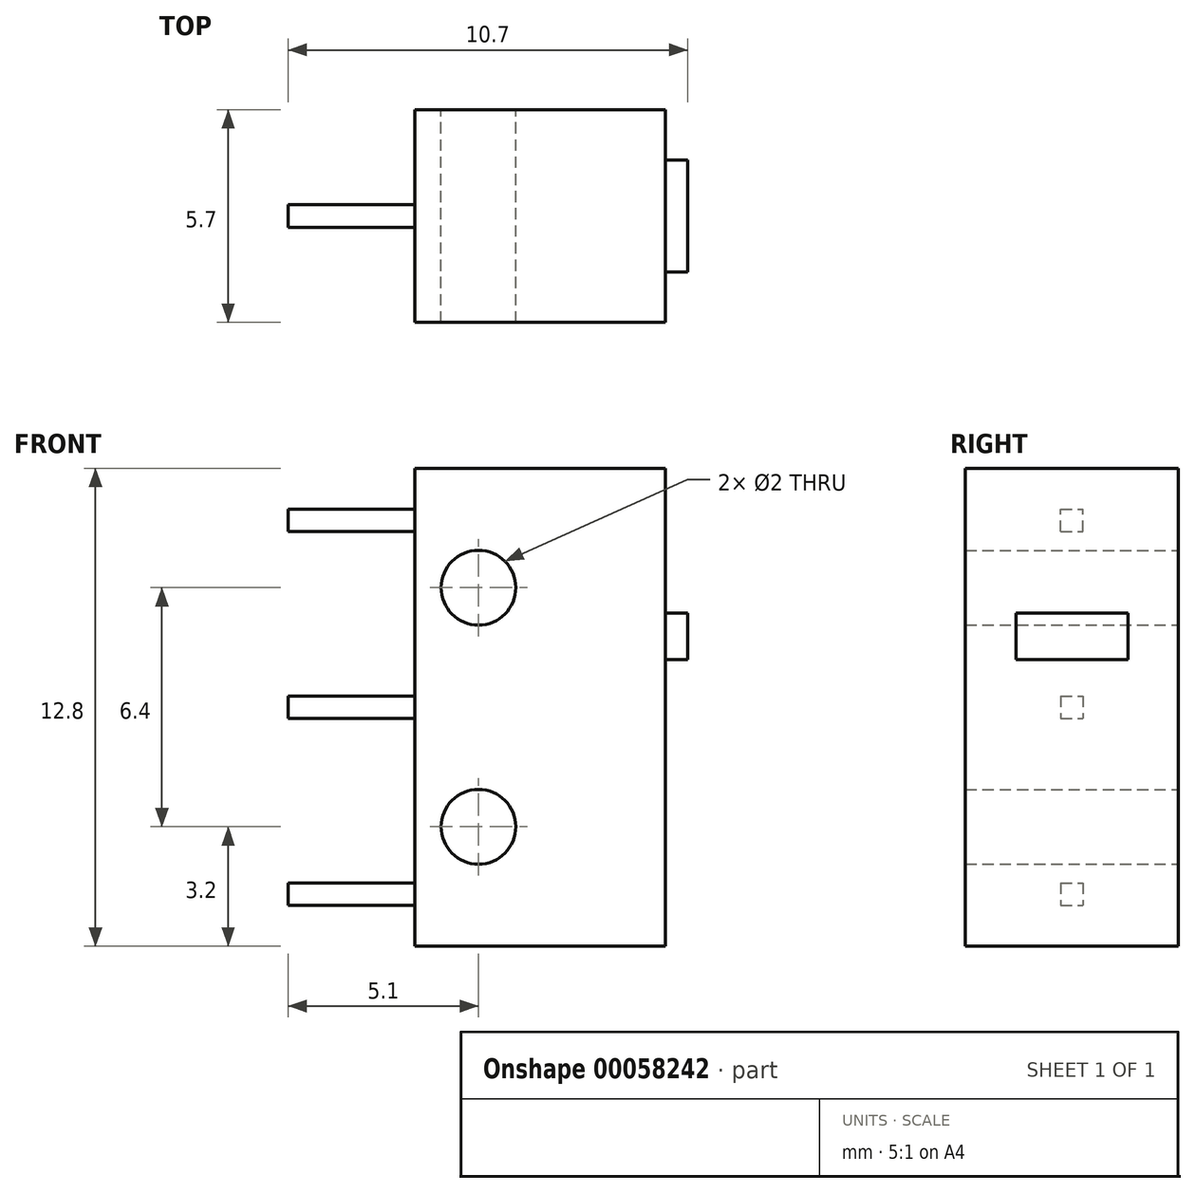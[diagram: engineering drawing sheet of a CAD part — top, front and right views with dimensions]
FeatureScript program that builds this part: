
annotation { "Feature Type Name" : "Feature", "Feature Type Description" : "" }
export const myFeature = defineFeature(function(context is Context, id is Id, definition is map)
    precondition{}
    {
        {
            var Q0;
            Q0=qCreatedBy(makeId("Front.planeOp"),FACE);
            var sketch = newSketch(context, id + "F0", { "sketchPlane" : qUnion([Q0])});
            skLineSegment(sketch, "E0.bottom", {"start": v(3.35, 6.4) * mm, "end": v(-3.35, 6.4) * mm});
            skLineSegment(sketch, "E0.top", {"start": v(3.35, -6.4) * mm, "end": v(-3.35, -6.4) * mm});
            skLineSegment(sketch, "E0.left", {"start": v(3.35, 6.4) * mm, "end": v(3.35, -6.4) * mm});
            skLineSegment(sketch, "E0.right", {"start": v(-3.35, 6.4) * mm, "end": v(-3.35, -6.4) * mm});
            skPoint(sketch, "E0.middle", {"position": v(0, 0) * mm});
            skCircle(sketch, "E1", {"center": v(-1.65, 3.2) * mm, "radius": 1 * mm});
            skLineSegment(sketch, "E2", {"start": v(0, 0) * mm, "end": v(-3.35, 0) * mm, "construction": true});
            skCircle(sketch, "E3.MirrorC", {"center": v(-1.65, -3.2) * mm, "radius": 1 * mm});
            skSolve(sketch);
        }
        {
            var Q0;
            Q0 = qSketchRegion(id + "F0", true);
            extrude(context, id + "F1", {"entities" : qUnion([Q0]), "depth" : 5.7 * mm, "symmetric" : true});
        }
        {
            var Q0;
            Q0=makeQuery(id+"F1.opExtrude","SWEPT_FACE",FACE,{"disambiguationData":[OSD([sQuery(id+"F0.wireOp",EDGE,"E0.right")])]});
            var sketch = newSketch(context, id + "F2", { "sketchPlane" : qUnion([Q0])});
            skLineSegment(sketch, "E4", {"start": v(0, 6.4) * mm, "end": v(0, 0) * mm, "construction": true});
            skLineSegment(sketch, "E5", {"start": v(0, 0) * mm, "end": v(2.85, 0) * mm, "construction": true});
            skLineSegment(sketch, "E6.bottom", {"start": v(0.3, 0.3) * mm, "end": v(-0.3, 0.3) * mm});
            skLineSegment(sketch, "E6.top", {"start": v(0.3, -0.3) * mm, "end": v(-0.3, -0.3) * mm});
            skLineSegment(sketch, "E6.left", {"start": v(0.3, 0.3) * mm, "end": v(0.3, -0.3) * mm});
            skLineSegment(sketch, "E6.right", {"start": v(-0.3, 0.3) * mm, "end": v(-0.3, -0.3) * mm});
            skPoint(sketch, "E6.middle", {"position": v(0, 0) * mm});
            skLineSegment(sketch, "E7.bottom", {"start": v(0.3, 4.7) * mm, "end": v(-0.3, 4.7) * mm});
            skLineSegment(sketch, "E7.top", {"start": v(0.3, 5.3) * mm, "end": v(-0.3, 5.3) * mm});
            skLineSegment(sketch, "E7.left", {"start": v(0.3, 4.7) * mm, "end": v(0.3, 5.3) * mm});
            skLineSegment(sketch, "E7.right", {"start": v(-0.3, 4.7) * mm, "end": v(-0.3, 5.3) * mm});
            skPoint(sketch, "E7.middle", {"position": v(0, 5) * mm});
            skLineSegment(sketch, "E8.MirrorCS", {"start": v(0.3, -5.3) * mm, "end": v(-0.3, -5.3) * mm});
            skLineSegment(sketch, "E9.MirrorCS", {"start": v(0.3, -4.7) * mm, "end": v(0.3, -5.3) * mm});
            skLineSegment(sketch, "E10.MirrorCS", {"start": v(-0.3, -4.7) * mm, "end": v(-0.3, -5.3) * mm});
            skPoint(sketch, "E11.MirrorP", {"position": v(0, -5) * mm});
            skLineSegment(sketch, "E12.MirrorCS", {"start": v(0.3, -4.7) * mm, "end": v(-0.3, -4.7) * mm});
            skSolve(sketch);
        }
        {
            var Q0;
            Q0 = qSketchRegion(id + "F2", true);
            extrude(context, id + "F3", {"entities" : qUnion([Q0]), "operationType" : NewBodyOperationType.ADD, "depth" : 3.4 * mm});
        }
        {
            var Q0;
            Q0=makeQuery(id+"F1.opExtrude","SWEPT_FACE",FACE,{"disambiguationData":[OSD([sQuery(id+"F0.wireOp",EDGE,"E0.left")])]});
            var sketch = newSketch(context, id + "F4", { "sketchPlane" : qUnion([Q0])});
            skLineSegment(sketch, "E13", {"start": v(0, 6.4) * mm, "end": v(0, 1.9) * mm, "construction": true});
            skLineSegment(sketch, "E14.bottom", {"start": v(1.5, 2.53) * mm, "end": v(-1.5, 2.53) * mm});
            skLineSegment(sketch, "E14.top", {"start": v(1.5, 1.27) * mm, "end": v(-1.5, 1.27) * mm});
            skLineSegment(sketch, "E14.left", {"start": v(1.5, 2.53) * mm, "end": v(1.5, 1.27) * mm});
            skLineSegment(sketch, "E14.right", {"start": v(-1.5, 2.52) * mm, "end": v(-1.5, 1.27) * mm});
            skPoint(sketch, "E14.middle", {"position": v(0, 1.9) * mm});
            skSolve(sketch);
        }
        {
            var Q0;
            Q0 = qSketchRegion(id + "F4", true);
            extrude(context, id + "F5", {"entities" : qUnion([Q0]), "operationType" : NewBodyOperationType.ADD, "depth" : 0.6 * mm});
        }
    });
